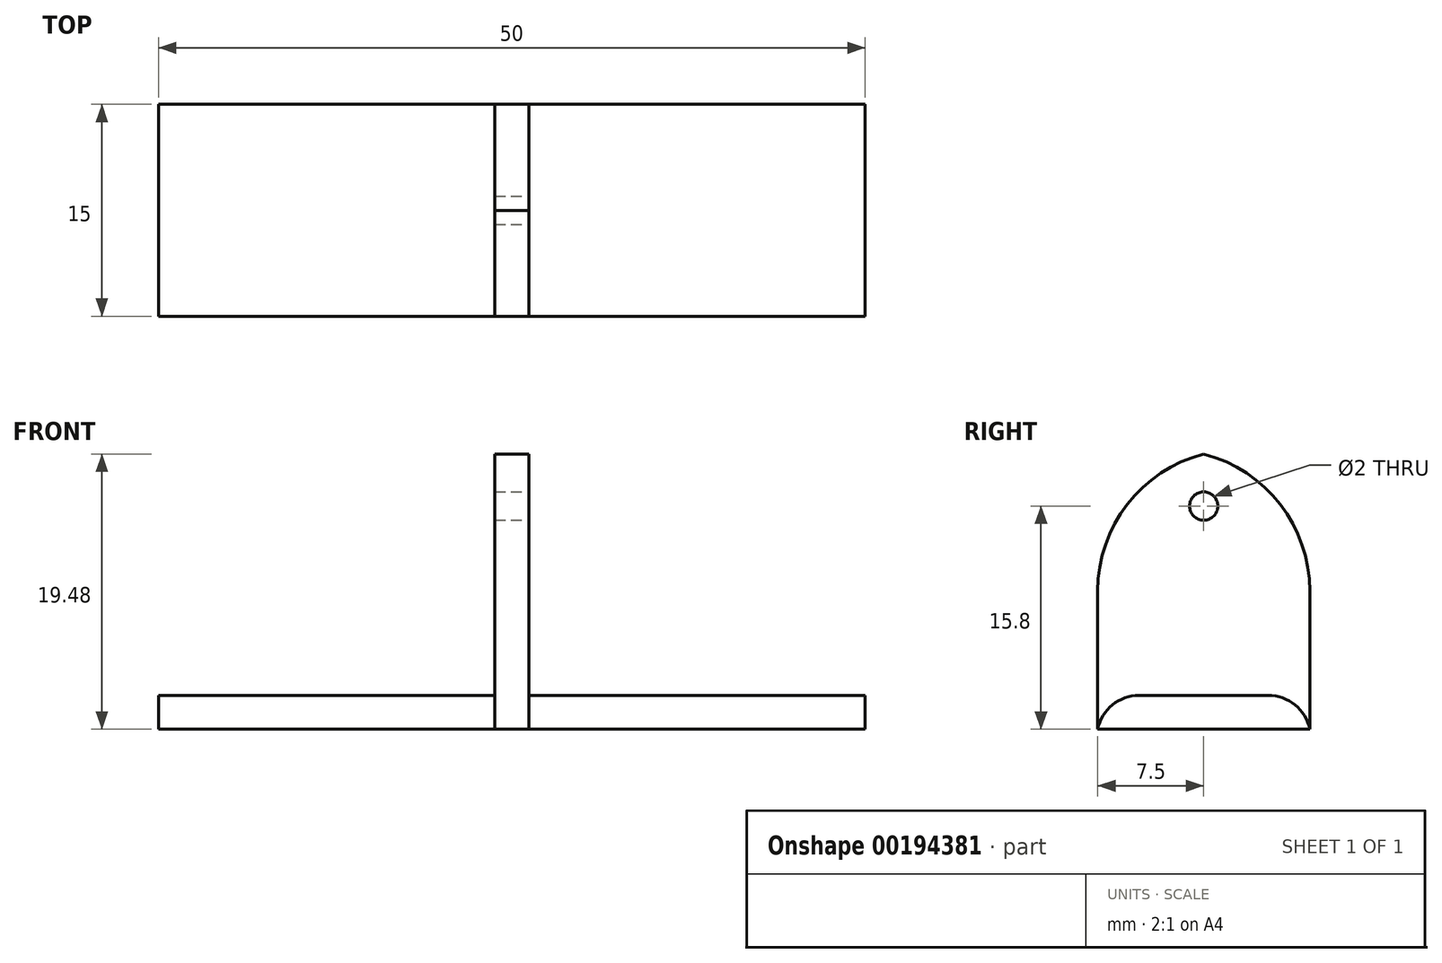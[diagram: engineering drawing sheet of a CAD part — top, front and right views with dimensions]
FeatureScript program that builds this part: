
annotation { "Feature Type Name" : "Feature", "Feature Type Description" : "" }
export const myFeature = defineFeature(function(context is Context, id is Id, definition is map)
    precondition{}
    {
        {
            var Q0;
            Q0=qCreatedBy(makeId("Top.planeOp"),FACE);
            var sketch = newSketch(context, id + "F0", { "sketchPlane" : qUnion([Q0])});
            skLineSegment(sketch, "E0.bottom", {"start": v(-25, 7.5) * mm, "end": v(25, 7.5) * mm});
            skLineSegment(sketch, "E0.top", {"start": v(-25, -7.5) * mm, "end": v(25, -7.5) * mm});
            skLineSegment(sketch, "E0.left", {"start": v(-25, 7.5) * mm, "end": v(-25, -7.5) * mm});
            skLineSegment(sketch, "E0.right", {"start": v(25, 7.5) * mm, "end": v(25, -7.5) * mm});
            skPoint(sketch, "E0.middle", {"position": v(0, 0) * mm});
            skSolve(sketch);
        }
        {
            assignVariable(context, id + "F1", {"name" : "pushRodHeight", "anyValue" : 15});
        }
        {
            var Q0;
            Q0 = qSketchRegion(id + "F0", true);
            extrude(context, id + "F2", {"entities" : qUnion([Q0]), "depth" : 2.4 * mm});
        }
        {
            var Q0;
            Q0=makeQuery(id+"F2.opExtrude","CAP_FACE",FACE,{"disambiguationData":[OSD([sQuery(id+"F0.wireOp",EDGE,"E0.bottom"),sQuery(id+"F0.wireOp",EDGE,"E0.top"),sQuery(id+"F0.wireOp",EDGE,"E0.left"),sQuery(id+"F0.wireOp",EDGE,"E0.right")])],"isStart":false});
            var sketch = newSketch(context, id + "F3", { "sketchPlane" : qUnion([Q0])});
            skLineSegment(sketch, "E1.bottom", {"start": v(-1.2, 7.5) * mm, "end": v(1.2, 7.5) * mm});
            skLineSegment(sketch, "E1.top", {"start": v(-1.2, -7.5) * mm, "end": v(1.2, -7.5) * mm});
            skLineSegment(sketch, "E1.left", {"start": v(-1.2, 7.5) * mm, "end": v(-1.2, -7.5) * mm});
            skLineSegment(sketch, "E1.right", {"start": v(1.2, 7.5) * mm, "end": v(1.2, -7.5) * mm});
            skPoint(sketch, "E1.middle", {"position": v(0, 0) * mm});
            skSolve(sketch);
        }
        {
            var Q0;
            Q0=makeQuery(id+"F3.imprint","IMPRINT",FACE,{"disambiguationData":[TD([[makeQuery(id+"F3.imprint","IMPRINT",EDGE,{"derivedFrom":sQuery(id+"F3.wireOp",EDGE,"E1.bottom")}),-1.0]])]});
            extrude(context, id + "F4", {"entities" : qUnion([Q0]), "operationType" : NewBodyOperationType.ADD, "depth" : (getVariable(context, 'pushRodHeight') + 2.4) * mm});
        }
        {
            var Q0;
            Q0=makeQuery(id+"F4.opExtrude","SWEPT_FACE",FACE,{"disambiguationData":[OSD([sQuery(id+"F3.wireOp",EDGE,"E1.right")])]});
            var sketch = newSketch(context, id + "F5", { "sketchPlane" : qUnion([Q0])});
            skCircle(sketch, "E2", {"center": v(0, 15.8) * mm, "radius": 1 * mm});
            skSolve(sketch);
        }
        {
            var Q0;
            Q0=makeQuery(id+"F4.opExtrude","CAP_EDGE",EDGE,{"disambiguationData":[OSD([sQuery(id+"F3.wireOp",EDGE,"E1.top")])],"isStart":false});
            var Q1;
            Q1=makeQuery(id+"F4.opExtrude","CAP_EDGE",EDGE,{"disambiguationData":[OSD([sQuery(id+"F3.wireOp",EDGE,"E1.bottom")])],"isStart":false});
            fillet(context, id + "F6", {"entities" : qUnion([Q0, Q1]), "radius" : 10 * mm, "tangentPropagation" : true, "allowEdgeOverflow" : false});
        }
        {
            var Q0;
            Q0 = qSketchRegion(id + "F5", true);
            extrude(context, id + "F7", {"entities" : qUnion([Q0]), "operationType" : NewBodyOperationType.REMOVE, "endBound" : BoundingType.THROUGH_ALL, "oppositeDirection" : true, "depth" : 25 * mm});
        }
        {
            var Q0;
            {var subQ0=sQuery(id+"F0.wireOp",EDGE,"E0.left");var subQ1=sQuery(id+"F0.wireOp",EDGE,"E0.top");Q0=makeQuery(id+"F4.boolean.opBoolean","SPLIT",EDGE,{"disambiguationData":[TD([makeQuery(id+"F2.opExtrude","SWEPT_FACE",FACE,{"disambiguationData":[OSD([subQ0])]})])],"derivedFrom":makeQuery(id+"F2.opExtrude","CAP_EDGE",EDGE,{"disambiguationData":[OSD([subQ1])],"isStart":false})});}
            var Q1;
            {var subQ0=sQuery(id+"F0.wireOp",EDGE,"E0.right");var subQ1=sQuery(id+"F0.wireOp",EDGE,"E0.top");Q1=makeQuery(id+"F4.boolean.opBoolean","SPLIT",EDGE,{"disambiguationData":[TD([makeQuery(id+"F2.opExtrude","SWEPT_FACE",FACE,{"disambiguationData":[OSD([subQ0])]})])],"derivedFrom":makeQuery(id+"F2.opExtrude","CAP_EDGE",EDGE,{"disambiguationData":[OSD([subQ1])],"isStart":false})});}
            var Q2;
            {var subQ0=sQuery(id+"F0.wireOp",EDGE,"E0.right");var subQ1=sQuery(id+"F0.wireOp",EDGE,"E0.bottom");Q2=makeQuery(id+"F4.boolean.opBoolean","SPLIT",EDGE,{"disambiguationData":[TD([makeQuery(id+"F2.opExtrude","SWEPT_FACE",FACE,{"disambiguationData":[OSD([subQ0])]})])],"derivedFrom":makeQuery(id+"F2.opExtrude","CAP_EDGE",EDGE,{"disambiguationData":[OSD([subQ1])],"isStart":false})});}
            var Q3;
            {var subQ0=sQuery(id+"F0.wireOp",EDGE,"E0.left");var subQ1=sQuery(id+"F0.wireOp",EDGE,"E0.bottom");Q3=makeQuery(id+"F4.boolean.opBoolean","SPLIT",EDGE,{"disambiguationData":[TD([makeQuery(id+"F2.opExtrude","SWEPT_FACE",FACE,{"disambiguationData":[OSD([subQ0])]})])],"derivedFrom":makeQuery(id+"F2.opExtrude","CAP_EDGE",EDGE,{"disambiguationData":[OSD([subQ1])],"isStart":false})});}
            fillet(context, id + "F8", {"entities" : qUnion([Q0, Q1, Q2, Q3]), "radius" : 3 * mm, "tangentPropagation" : true, "allowEdgeOverflow" : false});
        }
    });
